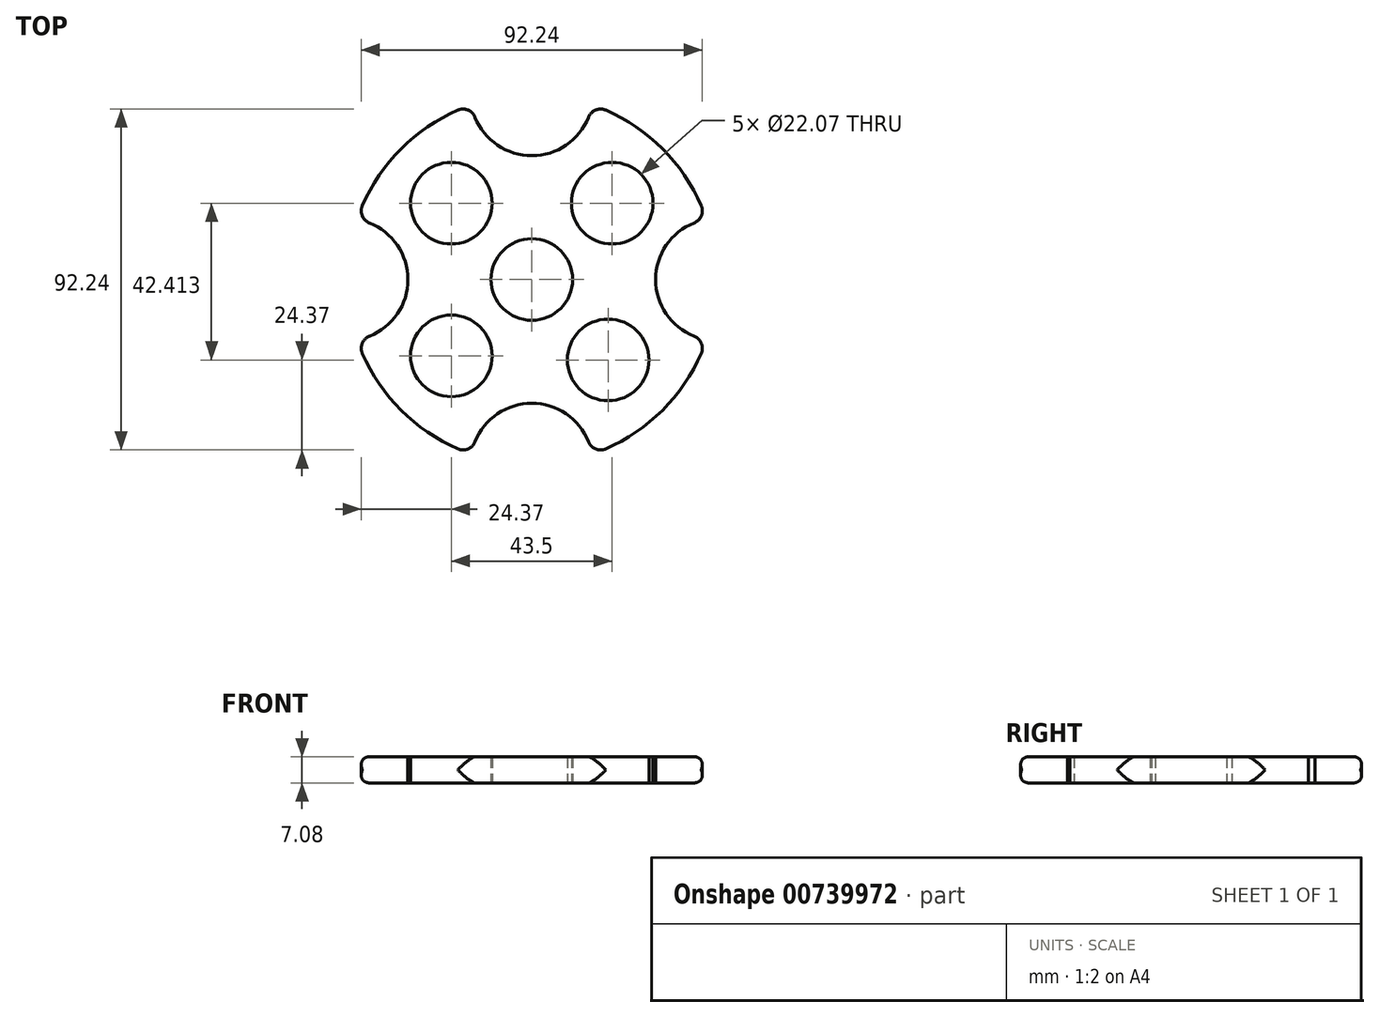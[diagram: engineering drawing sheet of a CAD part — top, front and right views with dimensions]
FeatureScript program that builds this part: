
annotation { "Feature Type Name" : "Feature", "Feature Type Description" : "" }
export const myFeature = defineFeature(function(context is Context, id is Id, definition is map)
    precondition{}
    {
        {
            var Q0;
            Q0=qCreatedBy(makeId("Top.planeOp"),FACE);
            var sketch = newSketch(context, id + "F0", { "sketchPlane" : qUnion([Q0])});
            skCircle(sketch, "E0", {"center": v(0, 0) * mm, "radius": 50 * mm});
            skPoint(sketch, "E1", {"position": v(0, 50) * mm});
            skPoint(sketch, "E2", {"position": v(50, 0) * mm});
            skPoint(sketch, "E3", {"position": v(0, -50) * mm});
            skPoint(sketch, "E4", {"position": v(-50, 0) * mm});
            skPoint(sketch, "E5", {"position": v(-21.75, 20.66) * mm});
            skPoint(sketch, "E6", {"position": v(21.75, 20.66) * mm});
            skPoint(sketch, "E7", {"position": v(-21.75, -20.66) * mm});
            skPoint(sketch, "E8", {"position": v(135.13, 18.48) * mm});
            skPoint(sketch, "E9", {"position": v(20.66, -21.75) * mm});
            skSolve(sketch);
        }
        {
            var Q0;
            Q0=makeQuery(id+"F0.imprint","IMPRINT",FACE,{"disambiguationData":[TD([[makeQuery(id+"F0.imprint","IMPRINT",EDGE,{"derivedFrom":sQuery(id+"F0.wireOp",EDGE,"E0")}),1.0]])]});
            extrude(context, id + "F1", {"entities" : qUnion([Q0]), "depth" : 7.08 * mm, "offsetDistance" : 25 * mm});
        }
        {
            var Q0;
            Q0=sQuery(id+"F0.wireOp",VERTEX,"E0.center");
            var Q1;
            Q1=sQuery(id+"F0.wireOp",VERTEX,"E5");
            var Q2;
            Q2=sQuery(id+"F0.wireOp",VERTEX,"E6");
            var Q3;
            Q3=sQuery(id+"F0.wireOp",VERTEX,"E9");
            var Q4;
            Q4=sQuery(id+"F0.wireOp",VERTEX,"E7");
            var Q5;
            Q5=makeQuery(id+"F1.opExtrude","SWEPT_BODY",BODY,{"disambiguationData":[OSD([sQuery(id+"F0.wireOp",EDGE,"E0")])]});
            hole(context, id + "F2", {"style" : HoleStyle.SIMPLE, "endStyle" : HoleEndStyle.BLIND, "oppositeDirection" : true, "holeDiameter" : 22.07 * mm, "majorDiameter" : 5 * mm, "holeDepth" : 35.38 * mm, "isTappedThrough" : true, "tappedDepth" : 12 * mm, "tapClearance" : 3, "locations" : qUnion([Q0, Q1, Q2, Q3, Q4]), "scope" : qUnion([Q5])});
        }
        {
            var Q0;
            Q0=sQuery(id+"F0.wireOp",VERTEX,"E3");
            var Q1;
            Q1=sQuery(id+"F0.wireOp",VERTEX,"E4");
            var Q2;
            Q2=sQuery(id+"F0.wireOp",VERTEX,"E1");
            var Q3;
            Q3=sQuery(id+"F0.wireOp",VERTEX,"E2");
            var Q4;
            Q4=makeQuery(id+"F1.opExtrude","SWEPT_BODY",BODY,{"disambiguationData":[OSD([sQuery(id+"F0.wireOp",EDGE,"E0")])]});
            hole(context, id + "F3", {"style" : HoleStyle.SIMPLE, "endStyle" : HoleEndStyle.BLIND, "oppositeDirection" : true, "holeDiameter" : 33 * mm, "majorDiameter" : 5 * mm, "holeDepth" : 35.38 * mm, "isTappedThrough" : true, "tappedDepth" : 12 * mm, "tapClearance" : 3, "locations" : qUnion([Q0, Q1, Q2, Q3]), "scope" : qUnion([Q4])});
        }
        {
            var Q0;
            Q0=makeQuery(id+"F3.hole-2.boolean.opBoolean","COPY",FACE,{"derivedFrom":makeQuery(id+"F3.hole-2.opRevolve","SWEPT_FACE",FACE,{"disambiguationData":[OSD([sQuery(id+"F3.hole-2.sketch.wireOp",EDGE,"core_line_2")])]})});
            var Q1;
            {var subQ0=sQuery(id+"F0.wireOp",EDGE,"E0");var subQ3=makeQuery(id+"F3.hole-2.opRevolve","SWEPT_FACE",FACE,{"disambiguationData":[OSD([sQuery(id+"F3.hole-2.sketch.wireOp",EDGE,"core_line_2")])]});Q1=makeQuery(id+"F3.hole-3.boolean.opBoolean","SPLIT",FACE,{"disambiguationData":[TD([makeQuery(id+"F3.hole-2.boolean.opBoolean","COPY",FACE,{"derivedFrom":subQ3})])],"derivedFrom":makeQuery(id+"F3.hole-2.boolean.opBoolean","SPLIT",FACE,{"disambiguationData":[TD([makeQuery(id+"F3.hole-0.boolean.opBoolean","COPY",FACE,{"derivedFrom":makeQuery(id+"F3.hole-0.opRevolve","SWEPT_FACE",FACE,{"disambiguationData":[OSD([sQuery(id+"F3.hole-0.sketch.wireOp",EDGE,"core_line_2")])]})})])],"derivedFrom":makeQuery(id+"F3.hole-1.boolean.opBoolean","SPLIT",FACE,{"disambiguationData":[OD(1.0)],"derivedFrom":makeQuery(id+"F1.opExtrude","SWEPT_FACE",FACE,{"disambiguationData":[OSD([subQ0])]})})})});}
            var Q2;
            {var subQ0=sQuery(id+"F0.wireOp",EDGE,"E0");Q2=makeQuery(id+"F3.hole-2.boolean.opBoolean","SPLIT",FACE,{"disambiguationData":[TD([makeQuery(id+"F3.hole-1.boolean.opBoolean","COPY",FACE,{"derivedFrom":makeQuery(id+"F3.hole-1.opRevolve","SWEPT_FACE",FACE,{"disambiguationData":[OSD([sQuery(id+"F3.hole-1.sketch.wireOp",EDGE,"core_line_2")])]})})])],"derivedFrom":makeQuery(id+"F3.hole-1.boolean.opBoolean","SPLIT",FACE,{"disambiguationData":[OD(1.0)],"derivedFrom":makeQuery(id+"F1.opExtrude","SWEPT_FACE",FACE,{"disambiguationData":[OSD([subQ0])]})})});}
            var Q3;
            Q3=makeQuery(id+"F3.hole-0.boolean.opBoolean","COPY",FACE,{"derivedFrom":makeQuery(id+"F3.hole-0.opRevolve","SWEPT_FACE",FACE,{"disambiguationData":[OSD([sQuery(id+"F3.hole-0.sketch.wireOp",EDGE,"core_line_2")])]})});
            var Q4;
            {var subQ0=sQuery(id+"F0.wireOp",EDGE,"E0");var subQ3=makeQuery(id+"F3.hole-0.boolean.opBoolean","COPY",FACE,{"derivedFrom":makeQuery(id+"F3.hole-0.opRevolve","SWEPT_FACE",FACE,{"disambiguationData":[OSD([sQuery(id+"F3.hole-0.sketch.wireOp",EDGE,"core_line_2")])]})});Q4=makeQuery(id+"F3.hole-3.boolean.opBoolean","SPLIT",FACE,{"disambiguationData":[TD([subQ3])],"derivedFrom":makeQuery(id+"F3.hole-2.boolean.opBoolean","SPLIT",FACE,{"disambiguationData":[TD([subQ3])],"derivedFrom":makeQuery(id+"F3.hole-1.boolean.opBoolean","SPLIT",FACE,{"disambiguationData":[OD(1.0)],"derivedFrom":makeQuery(id+"F1.opExtrude","SWEPT_FACE",FACE,{"disambiguationData":[OSD([subQ0])]})})})});}
            var Q5;
            Q5=makeQuery(id+"F3.hole-1.boolean.opBoolean","SPLIT",FACE,{"disambiguationData":[OD(0.0)],"derivedFrom":makeQuery(id+"F1.opExtrude","SWEPT_FACE",FACE,{"disambiguationData":[OSD([sQuery(id+"F0.wireOp",EDGE,"E0")])]})});
            var Q6;
            Q6=makeQuery(id+"F3.hole-3.boolean.opBoolean","COPY",FACE,{"derivedFrom":makeQuery(id+"F3.hole-3.opRevolve","SWEPT_FACE",FACE,{"disambiguationData":[OSD([sQuery(id+"F3.hole-3.sketch.wireOp",EDGE,"core_line_2")])]})});
            var Q7;
            Q7=makeQuery(id+"F3.hole-1.boolean.opBoolean","COPY",FACE,{"derivedFrom":makeQuery(id+"F3.hole-1.opRevolve","SWEPT_FACE",FACE,{"disambiguationData":[OSD([sQuery(id+"F3.hole-1.sketch.wireOp",EDGE,"core_line_2")])]})});
            fillet(context, id + "F4", {"entities" : qUnion([Q0, Q1, Q2, Q3, Q4, Q5, Q6, Q7]), "radius" : 3.5 * mm, "tangentPropagation" : true, "allowEdgeOverflow" : false});
        }
    });
